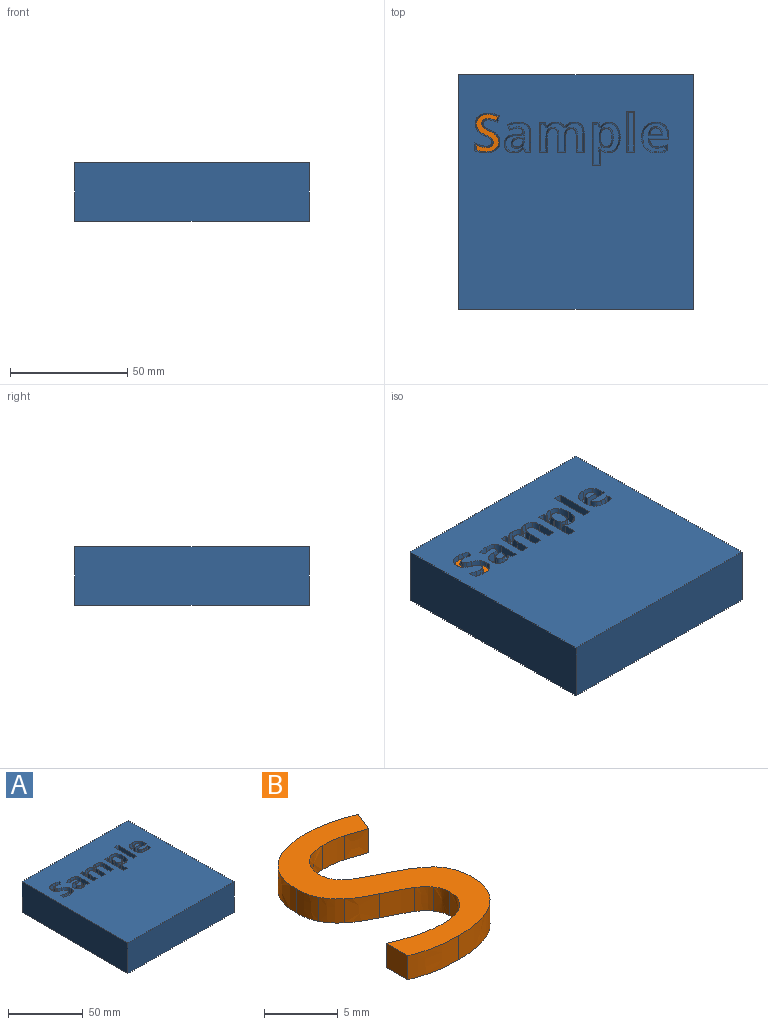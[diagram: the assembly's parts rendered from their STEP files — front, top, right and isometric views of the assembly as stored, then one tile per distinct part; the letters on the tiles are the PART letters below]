
ASSEMBLY  parts=2 mates=1
PART A: 143 faces, bbox 101x101x26 mm
  f0: plane 100.69x100.69mm, normal (0,0,1), area 9312.7mm2, adj f1,f2,f3,f4,f10,f11,f12,f13
  f1: plane 100x25mm, normal (-1,0,0), area 2500mm2, adj f0,f2,f4,f5
  f2: plane 100x25mm, normal (0,-1,0), area 2500mm2, adj f0,f1,f3,f5
  f3: plane 100x25mm, normal (1,0,0), area 2500mm2, adj f0,f2,f4,f5
  f4: plane 100x25mm, normal (0,1,0), area 2500mm2, adj f0,f1,f3,f5
  f5: plane 100x100mm, normal (0,0,-1), area 10000mm2, adj f1,f2,f3,f4
  f6: bspline ~4x2.15mm, area 8.7mm2, adj f7,f25,f26,f142
  f7: bspline ~4.8x3.02mm, area 10.5mm2, adj f6,f8,f26,f142
  f8: plane 6.04x4.03mm, normal (0,-0.99,0.14), area 21.9mm2, adj f7,f9,f26,f142
  f9: bspline ~4.8x3.01mm, area 10.5mm2, adj f8,f25,f26,f142
  f10: bspline ~4.8x2.51mm, area 9.9mm2, adj f0,f11,f24,f26
  f11: bspline ~4x2.05mm, area 7.3mm2, adj f0,f10,f12,f26
  f12: plane 4.01x2.68mm, normal (-0.99,0,0.14), area 8.3mm2, adj f0,f11,f13,f26
  f13: bspline ~4.8x2.41mm, area 7.6mm2, adj f0,f12,f14,f26
  f14: bspline ~4.8x2.31mm, area 9mm2, adj f0,f13,f15,f26
  f15: bspline ~4.8x2.76mm, area 11mm2, adj f0,f14,f16,f26
  f16: bspline ~4.8x3.36mm, area 12.1mm2, adj f0,f15,f17,f26
  f17: plane 8.75x4.03mm, normal (0,0.99,0.14), area 32.9mm2, adj f0,f16,f18,f26
  f18: plane 4x1.67mm, normal (-0.99,0,0.14), area 5.6mm2, adj f0,f17,f19,f26
  f19: bspline ~4.8x4.21mm, area 17.6mm2, adj f0,f18,f20,f26
  f20: bspline ~4.16x4mm, area 17.5mm2, adj f0,f19,f21,f26
  f21: bspline ~4.8x4.39mm, area 18.7mm2, adj f0,f20,f22,f26
  f22: bspline ~4.91x4mm, area 20.5mm2, adj f0,f21,f23,f26
  f23: bspline ~4.8x4.77mm, area 20.1mm2, adj f0,f22,f24,f26
  f24: bspline ~4.76x4mm, area 20.1mm2, adj f0,f10,f23,f26
  f25: bspline ~4.8x2.22mm, area 8.7mm2, adj f6,f9,f26,f142
  f26: plane 12.46x11mm, normal (0,0,1), area 57.4mm2, adj f6,f7,f8,f9,f10,f11,f12,f13
  f27: plane 6.34x4mm, normal (-0.99,0,0.14), area 24.5mm2, adj f0,f28,f54,f55
  f28: bspline ~4.8x3.25mm, area 12.7mm2, adj f0,f27,f29,f55
  f29: bspline ~4x2.35mm, area 9.9mm2, adj f0,f28,f30,f55
  f30: bspline ~4x1.91mm, area 7.8mm2, adj f0,f29,f31,f55
  f31: bspline ~4.8x2.42mm, area 9.3mm2, adj f0,f30,f32,f55
  f32: plane 7.38x4mm, normal (0.99,0,0.14), area 28.7mm2, adj f0,f31,f33,f55
  f33: plane 4x3.45mm, normal (0,0.99,0.14), area 11.7mm2, adj f0,f32,f34,f55
  f34: plane 8.23x4mm, normal (-0.99,0,0.14), area 32.1mm2, adj f0,f33,f35,f55
  f35: bspline ~4.8x3.53mm, area 14.4mm2, adj f0,f34,f36,f55
  f36: bspline ~4.8x3.25mm, area 13.3mm2, adj f0,f35,f37,f55
  f37: bspline ~4.8x2.23mm, area 8.8mm2, adj f0,f36,f38,f55
  f38: bspline ~4.8x2mm, area 8.3mm2, adj f0,f37,f39,f55
  f39: plane 4.03x0.99mm, normal (0,-0.99,0.14), area 2.6mm2, adj f0,f38,f40,f55
  f40: bspline ~4.8x4.04mm, area 17.6mm2, adj f0,f39,f41,f55
  f41: bspline ~4.8x2.2mm, area 8.7mm2, adj f0,f40,f42,f55
  f42: bspline ~4x1.92mm, area 8.2mm2, adj f0,f41,f43,f55
  f43: plane 4.03x0.97mm, normal (0,-0.99,0.14), area 2.3mm2, adj f0,f42,f44,f55
  f44: plane 4x2.18mm, normal (-0.95,-0.27,0.14), area 6.8mm2, adj f0,f43,f45,f55
  f45: plane 4x2.63mm, normal (0,-0.99,0.14), area 8.6mm2, adj f0,f44,f46,f55
  f46: plane 12.63x4mm, normal (0.99,0,0.14), area 48.7mm2, adj f0,f45,f47,f55
  f47: plane 4x3.44mm, normal (0,0.99,0.14), area 11.6mm2, adj f0,f46,f48,f55
  f48: plane 5.94x4mm, normal (-0.99,0,0.14), area 22.9mm2, adj f0,f47,f49,f55
  f49: bspline ~4x3.49mm, area 13.9mm2, adj f0,f48,f50,f55
  f50: bspline ~4.8x2.5mm, area 10.3mm2, adj f0,f49,f51,f55
  f51: bspline ~4x1.91mm, area 7.8mm2, adj f0,f50,f52,f55
  f52: bspline ~4.8x2.42mm, area 9.3mm2, adj f0,f51,f53,f55
  f53: plane 7.38x4mm, normal (0.99,0,0.14), area 28.7mm2, adj f0,f52,f54,f55
  f54: plane 4x3.44mm, normal (0,0.99,0.14), area 11.6mm2, adj f0,f27,f53,f55
  f55: plane 18.61x12.29mm, normal (0,0,1), area 95.5mm2, adj f27,f28,f29,f30,f31,f32,f33,f34
  f56: plane 17.57x4mm, normal (-0.99,0,0.14), area 68.7mm2, adj f0,f57,f59,f60
  f57: plane 4x3.44mm, normal (0,-0.99,0.14), area 11.6mm2, adj f0,f56,f58,f60
  f58: plane 17.57x4mm, normal (0.99,0,0.14), area 68.7mm2, adj f0,f57,f59,f60
  f59: plane 4x3.44mm, normal (0,0.99,0.14), area 11.6mm2, adj f0,f56,f58,f60
  f60: plane 16.45x2.32mm, normal (0,0,1), area 38.2mm2, adj f56,f57,f58,f59
  f61: plane 4x2.4mm, normal (0,0.99,0.14), area 7.8mm2, adj f0,f62,f85,f86
  f62: plane 8.41x4mm, normal (-0.99,0,0.14), area 32.8mm2, adj f0,f61,f63,f86
  f63: bspline ~4.8x3.37mm, area 14.2mm2, adj f0,f62,f64,f86
  f64: bspline ~4x3.9mm, area 15.9mm2, adj f0,f63,f65,f86
  f65: bspline ~4.83x4.8mm, area 18.6mm2, adj f0,f64,f66,f86
  f66: plane 4.02x2.34mm, normal (0.89,0.44,0.14), area 8.3mm2, adj f0,f65,f67,f86
  f67: bspline ~4.8x3.83mm, area 14.3mm2, adj f0,f66,f68,f86
  f68: bspline ~4.8x2.64mm, area 14.5mm2, adj f0,f67,f69,f86
  f69: plane 4x1.1mm, normal (0.99,0,0.14), area 3.3mm2, adj f0,f68,f70,f86
  f70: plane 4x2.76mm, normal (0.03,-0.99,0.14), area 10mm2, adj f0,f69,f71,f86
  f71: bspline ~4.8x4.26mm, area 17.2mm2, adj f0,f70,f72,f86
  f72: bspline ~4.8x2.96mm, area 12.7mm2, adj f0,f71,f73,f86
  f73: bspline ~4x2.96mm, area 12.1mm2, adj f0,f72,f74,f86
  f74: bspline ~4.8x2.86mm, area 11.7mm2, adj f0,f73,f75,f86
  f75: bspline ~4.8x2.4mm, area 9.4mm2, adj f0,f74,f76,f86
  f76: bspline ~4.8x2.26mm, area 9.6mm2, adj f0,f75,f77,f86
  f77: plane 4.01x0.76mm, normal (0,0.99,0.14), area 1.7mm2, adj f0,f76,f85,f86
  f78: plane 4x1.62mm, normal (0.99,0,0.14), area 5.4mm2, adj f79,f84,f86,f87
  f79: bspline ~4x2.23mm, area 9.1mm2, adj f78,f80,f86,f87
  f80: bspline ~4.8x2.39mm, area 9.3mm2, adj f79,f81,f86,f87
  f81: bspline ~4.8x2.34mm, area 12.1mm2, adj f80,f82,f86,f87
  f82: bspline ~4.8x2.07mm, area 8.2mm2, adj f81,f83,f86,f87
  f83: bspline ~4.8x2.62mm, area 10.1mm2, adj f82,f84,f86,f87
  f84: plane 4x1.91mm, normal (-0.03,0.99,0.14), area 6.6mm2, adj f78,f83,f86,f87
  f85: plane 4x2.28mm, normal (0.92,0.36,0.14), area 7.4mm2, adj f0,f61,f77,f86
  f86: plane 12.64x10.78mm, normal (0,0,1), area 58.4mm2, adj f61,f62,f63,f64,f65,f66,f67,f68
  f87: plane 4.62x3.88mm, normal (0,0,1), area 12.4mm2, adj f78,f79,f80,f81,f82,f83,f84
  f88: bspline ~4.8x2.57mm, area 10.3mm2, adj f0,f89,f110,f111
  f89: bspline ~4x2.48mm, area 10.9mm2, adj f0,f88,f90,f111
  f90: bspline ~4.8x3.51mm, area 14mm2, adj f0,f89,f91,f111
  f91: bspline ~4.8x4.8mm, area 19.7mm2, adj f0,f90,f92,f111
  f92: bspline ~4x3.5mm, area 15.4mm2, adj f0,f91,f93,f111
  f93: bspline ~4.8x3.78mm, area 16.6mm2, adj f0,f92,f94,f111
  f94: plane 4.02x0.9mm, normal (0,-0.99,0.14), area 2.1mm2, adj f0,f93,f95,f111
  f95: plane 4x2.2mm, normal (-0.95,-0.28,0.14), area 6.9mm2, adj f0,f94,f96,f111
  f96: plane 4x2.8mm, normal (0,-0.99,0.14), area 9.3mm2, adj f0,f95,f97,f111
  f97: plane 18.18x4mm, normal (0.99,0,0.14), area 71.2mm2, adj f0,f96,f98,f111
  f98: plane 4x3.44mm, normal (0,0.99,0.14), area 11.6mm2, adj f0,f97,f99,f111
  f99: plane 5.12x4mm, normal (-0.99,0,0.14), area 19.5mm2, adj f0,f98,f100,f111
  f100: bspline ~4.61x2.48mm, area 8.6mm2, adj f0,f99,f101,f111
  f101: plane 4.02x1.1mm, normal (0,0.99,0.14), area 2.6mm2, adj f0,f100,f110,f111
  f102: bspline ~4x2.27mm, area 9.7mm2, adj f103,f109,f111,f112
  f103: bspline ~4.8x3.15mm, area 12.3mm2, adj f102,f104,f111,f112
  f104: bspline ~4.8x4.49mm, area 22.1mm2, adj f103,f105,f111,f112
  f105: bspline ~4.8x2.47mm, area 10mm2, adj f104,f106,f111,f112
  f106: bspline ~4.8x3.29mm, area 12.9mm2, adj f105,f107,f111,f112
  f107: plane 4x0.56mm, normal (-0.99,0,0.14), area 1.5mm2, adj f106,f108,f111,f112
  f108: bspline ~4.8x3.03mm, area 11.6mm2, adj f107,f109,f111,f112
  f109: bspline ~4.8x2.41mm, area 9.6mm2, adj f102,f108,f111,f112
  f110: bspline ~4.8x3.7mm, area 15.7mm2, adj f0,f88,f101,f111
  f111: plane 18.26x11.63mm, normal (0,0,1), area 80.1mm2, adj f88,f89,f90,f91,f92,f93,f94,f95
  f112: plane 8.51x5.8mm, normal (0,0,1), area 30.8mm2, adj f102,f103,f104,f105,f106,f107,f108,f109
  f113: bspline ~4.8x2.73mm, area 11mm2, adj f0,f114,f140,f141
  f114: bspline ~4.8x3.47mm, area 15.2mm2, adj f0,f113,f115,f141
  f115: bspline ~4.8x2.6mm, area 10.3mm2, adj f0,f114,f116,f141
  f116: bspline ~4x1.16mm, area 4.3mm2, adj f0,f115,f117,f141
  f117: bspline ~4x1.11mm, area 4.1mm2, adj f0,f116,f118,f141
  f118: bspline ~4x1.63mm, area 6.5mm2, adj f0,f117,f119,f141
  f119: bspline ~4.8x1.97mm, area 7.4mm2, adj f0,f118,f120,f141
  f120: bspline ~4x1.83mm, area 7.2mm2, adj f0,f119,f121,f141
  f121: bspline ~4.8x2.44mm, area 8.4mm2, adj f0,f120,f122,f141
  f122: plane 4.01x2.74mm, normal (-0.92,0.38,0.14), area 9.7mm2, adj f0,f121,f123,f141
  f123: bspline ~4.8x2.61mm, area 9.2mm2, adj f0,f122,f124,f141
  f124: bspline ~4.8x2.46mm, area 9.7mm2, adj f0,f123,f125,f141
  f125: bspline ~4.8x4.11mm, area 16.9mm2, adj f0,f124,f126,f141
  f126: bspline ~4x3.45mm, area 14.7mm2, adj f0,f125,f127,f141
  f127: bspline ~4.8x2.03mm, area 7.9mm2, adj f0,f126,f128,f141
  f128: bspline ~4.8x1.84mm, area 7.5mm2, adj f0,f127,f129,f141
  f129: bspline ~4.8x2.58mm, area 10.4mm2, adj f0,f128,f130,f141
  f130: bspline ~4.8x2.55mm, area 9.9mm2, adj f0,f129,f131,f141
  f131: bspline ~4.8x1.35mm, area 4.8mm2, adj f0,f130,f132,f141
  f132: bspline ~4x1.19mm, area 4.4mm2, adj f0,f131,f133,f141
  f133: bspline ~4.8x1.86mm, area 7.2mm2, adj f0,f132,f134,f141
  f134: bspline ~4.8x2.16mm, area 8.2mm2, adj f0,f133,f135,f141
  f135: bspline ~4.8x2.29mm, area 9mm2, adj f0,f134,f136,f141
  f136: bspline ~4.8x3.1mm, area 10.6mm2, adj f0,f135,f137,f141
  f137: plane 4.01x3.26mm, normal (0.99,0,0.14), area 10.7mm2, adj f0,f136,f138,f141
  f138: bspline ~4.8x4.68mm, area 18.3mm2, adj f0,f137,f139,f141
  f139: bspline ~4.8x4.48mm, area 18.4mm2, adj f0,f138,f140,f141
  f140: bspline ~4x3.53mm, area 15.2mm2, adj f0,f113,f139,f141
  f141: plane 16.52x10.31mm, normal (0,0,1), area 64.2mm2, adj f113,f114,f115,f116,f117,f118,f119,f120
  f142: plane 5.02x2.84mm, normal (0,0,1), area 10.4mm2, adj f6,f7,f8,f9,f25
PART B: 30 faces, bbox 9.6x15.8x2 mm
  f0: extruded ~4.11x2mm, area 8.4mm2, adj f1,f27,f28,f29
  f1: extruded ~4.12x2mm, area 8.7mm2, adj f0,f2,f28,f29
  f2: extruded ~3.09x2mm, area 7mm2, adj f1,f3,f28,f29
  f3: extruded ~2.38x2mm, area 5.1mm2, adj f2,f4,f28,f29
  f4: extruded ~2.97x2.06mm, area 7.3mm2, adj f3,f5,f28,f29
  f5: extruded ~2.29x2mm, area 5.2mm2, adj f4,f6,f28,f29
  f6: extruded ~2x0.84mm, area 2.4mm2, adj f5,f7,f28,f29
  f7: extruded ~2x1.11mm, area 2.3mm2, adj f6,f8,f28,f29
  f8: extruded ~2x1.63mm, area 3.7mm2, adj f7,f9,f28,f29
  f9: extruded ~2x1.89mm, area 4.1mm2, adj f8,f10,f28,f29
  f10: extruded ~2x1.83mm, area 3.7mm2, adj f9,f11,f28,f29
  f11: extruded ~2x1.74mm, area 3.7mm2, adj f10,f12,f28,f29
  f12: plane 2x1.69mm, normal (0.92,-0.38,0), area 3.7mm2, adj f11,f13,f28,f29
  f13: extruded ~2x1.85mm, area 3.9mm2, adj f12,f14,f28,f29
  f14: extruded ~2.31x2mm, area 4.7mm2, adj f13,f15,f28,f29
  f15: extruded ~3.74x2mm, area 8mm2, adj f14,f16,f28,f29
  f16: extruded ~3.02x2mm, area 6.8mm2, adj f15,f17,f28,f29
  f17: extruded ~2x1.77mm, area 3.7mm2, adj f16,f18,f28,f29
  f18: extruded ~2x1.36mm, area 3.5mm2, adj f17,f19,f28,f29
  f19: extruded ~2.14x2mm, area 5mm2, adj f18,f20,f28,f29
  f20: extruded ~2.21x2mm, area 5mm2, adj f19,f21,f28,f29
  f21: extruded ~2x0.94mm, area 2.6mm2, adj f20,f22,f28,f29
  f22: extruded ~2x1.19mm, area 2.5mm2, adj f21,f23,f28,f29
  f23: extruded ~2x1.77mm, area 4.1mm2, adj f22,f24,f28,f29
  f24: extruded ~2.09x2mm, area 4.4mm2, adj f23,f25,f28,f29
  f25: extruded ~2.26x2mm, area 4.6mm2, adj f24,f26,f28,f29
  f26: extruded ~2.12x2mm, area 4.5mm2, adj f25,f27,f28,f29
  f27: plane 2.04x2mm, normal (-1,0,0), area 4.1mm2, adj f0,f26,f28,f29
  f28: plane 15.85x9.64mm, normal (0,0,1), area 64.2mm2, adj f0,f1,f2,f3,f4,f5,f6,f7
  f29: plane 15.85x9.64mm, normal (0,0,-1), area 64.2mm2, adj f0,f1,f2,f3,f4,f5,f6,f7
PLACE A t=(4.08,22,-12.02)mm
PLACE B t=(-25.04,39.27,9.12)mm
MATE slider A.f141 <-> B.f29  axis (0,0,1) through (-29.78,33.83,8.98)mm
